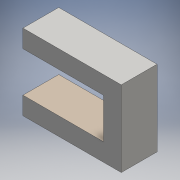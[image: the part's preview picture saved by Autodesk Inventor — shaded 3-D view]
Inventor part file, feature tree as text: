
AUTODESK INVENTOR PART (.ipt)
format: ipt  version: 2016 (Build 200138000, 138)  size: 99,328 bytes
history: native  units: in
note: dims shown in document units (in); Inventor stores cm internally (conversion verified against a paired STEP export)
features: other x5, sketch x1
ambient origin geometry x8: Origin, YZ Plane, XZ Plane, XY Plane, X Axis, Y Axis, Z Axis, Center Point
bodies: Solid1 (feature_tree)
feature tree (6):
  other  "chamber_conn_holder.ipt"
  other  "Solid1::chamber_conn_holder.ipt"
  other  "TaggingFeature1"
  sketch  "Sketch1"  dims[d0=0.3937in]
  other  "Srf1"
  other  "Srf1::Derived"
